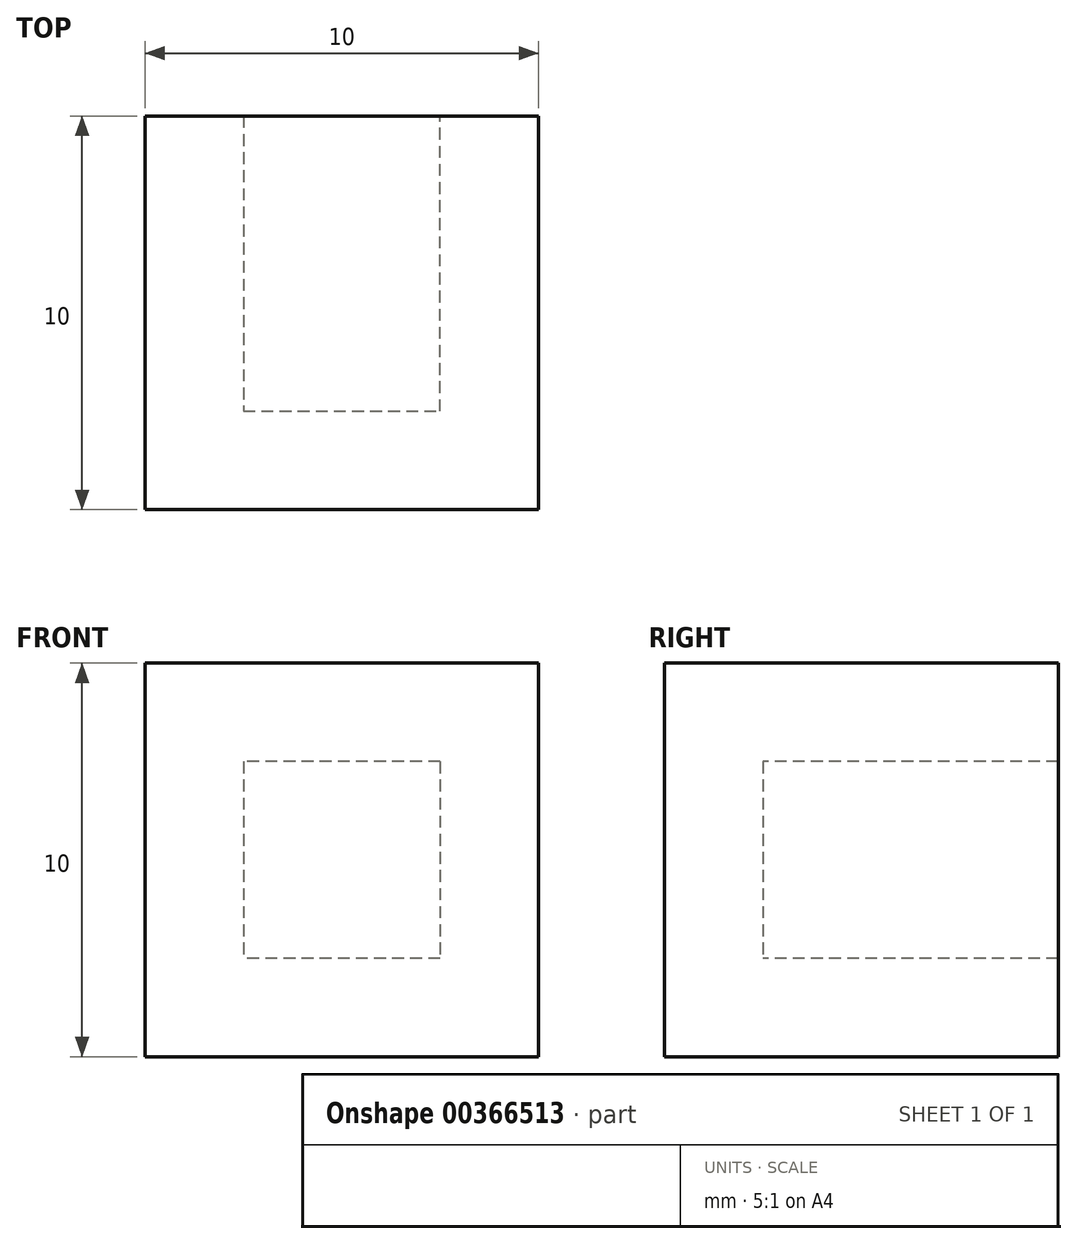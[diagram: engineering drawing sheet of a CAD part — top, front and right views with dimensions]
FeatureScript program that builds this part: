
annotation { "Feature Type Name" : "Feature", "Feature Type Description" : "" }
export const myFeature = defineFeature(function(context is Context, id is Id, definition is map)
    precondition{}
    {
        {
            var Q0;
            Q0=qCreatedBy(makeId("Top.planeOp"),FACE);
            var sketch = newSketch(context, id + "F0", { "sketchPlane" : qUnion([Q0])});
            skLineSegment(sketch, "E0", {"start": v(0, 0) * mm, "end": v(10, 0) * mm});
            skLineSegment(sketch, "E1", {"start": v(10, 0) * mm, "end": v(10, 10) * mm});
            skLineSegment(sketch, "E2", {"start": v(10, 10) * mm, "end": v(0, 10) * mm});
            skLineSegment(sketch, "E3", {"start": v(0, 10) * mm, "end": v(0, 0) * mm});
            skSolve(sketch);
        }
        {
            var Q0;
            Q0=qSketchRegion(id+"F0",true);
            extrude(context, id + "F1", {"entities" : qUnion([Q0]), "depth" : 10 * mm});
        }
        {
            var Q0;
            Q0=makeQuery(id+"F1.opExtrude","SWEPT_FACE",FACE,{"disambiguationData":[OSD([sQuery(id+"F0.wireOp",EDGE,"E2")])]});
            shell(context, id + "F2", {"entities" : qUnion([Q0]), "thickness" : 2.5 * mm});
        }
    });
